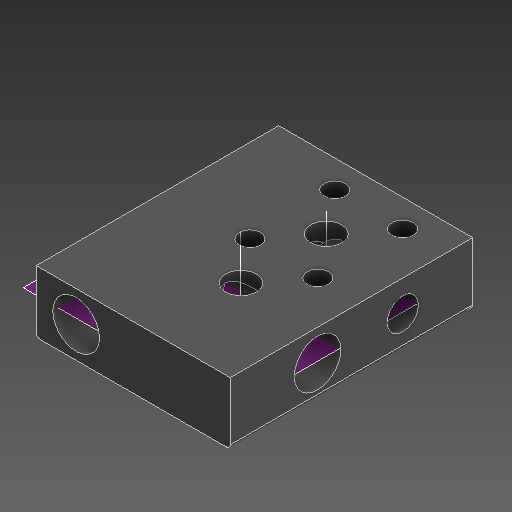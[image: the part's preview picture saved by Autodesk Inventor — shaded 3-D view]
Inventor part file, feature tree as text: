
AUTODESK INVENTOR PART (.ipt)
format: ipt  version: 2021 (Build 250183000, 183)  size: 205,312 bytes
history: native  units: in
note: dims shown in document units (in); Inventor stores cm internally (conversion verified against a paired STEP export)
features: other x6, sketch x4, plane x3
ambient origin geometry x8: Origin, YZ Plane, XZ Plane, XY Plane, X Axis, Y Axis, Z Axis, Center Point
bodies: Solid1 (feature_tree)
feature tree (13):
  other  "Val_BodV4.ipt"
  other  "Solid1::Val_BodV4.ipt"
  other  "TaggingFeature1"
  sketch  "Sketch3"  dims[d0=0.3937in]
  sketch  "Sketch5"
  sketch  "Sketch6"
  sketch  "Sketch4"
  plane  "Work Plane1"
  plane  "Work Plane2"
  plane  "Work Plane3"
  other  "Work Axis1"
  other  "Work Axis2"
  other  "Work Axis3"
